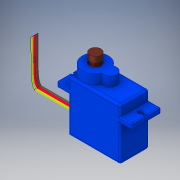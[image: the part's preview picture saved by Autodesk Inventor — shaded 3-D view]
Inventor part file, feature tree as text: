
AUTODESK INVENTOR PART (.ipt)
format: ipt  version: 2018 (Build 220112000, 112)  size: 405,504 bytes
history: native  units: in
note: dims shown in document units (in); Inventor stores cm internally (conversion verified against a paired STEP export)
features: sketch x10, extrude x9, fillet x2, plane x2, sweep x1
ambient origin geometry x8: Origin, YZ Plane, XZ Plane, XY Plane, X Axis, Y Axis, Z Axis, Center Point
bodies: Solid1 (feature_tree)
feature tree (24):
  extrude  "Servo_Body"  Depth=0.6102in
  extrude  "Cable_Opening"  Depth=0.0945in
  extrude  "GearBox_Housing"  Depth=0.4921in TaperAngle=0.0deg
  extrude  "Servo_Shaft"  Depth=0.0394in
  extrude  "GearBox_Housing_Extension"  Depth=0.4921in
  extrude  "Mounting_Holes"  Depth=0.0394in TaperAngle=0.0deg
  extrude  "Extrusion7"  Depth=0.189in
  fillet  "Fillet1"  Radius=0.1654in
  fillet  "Fillet2"  Radius=0.2205in
  extrude  "Cables"  Depth=0.1181in TaperAngle=0.0deg
  sweep  "Sweep1"
  plane  "Work Plane1"
  plane  "Work Plane2"
  extrude  "Shaft_Tapering"  Depth=0.0472in
  sketch  "Sketch1"  dims[d0=0.8898in d1=0.6102in]
  sketch  "Sketch2"  dims[d3=0.0945in d4=0.1969in]
  sketch  "Sketch4"  dims[d5=0.1732in d7=0.4921in d8=0.0in]
  sketch  "Sketch5"  dims[d9=0.1181in d10=0.0394in]
  sketch  "Sketch6"  dims[d11=0.1732in d12=0.4921in]
  sketch  "Sketch7"  dims[d13=0.2461in d14=0.0394in d15=0.0in]
  sketch  "Sketch8"  dims[d16=0.1654in d17=0.0in d18=0.189in d19=0.1654in d20=0.0in d21=0.2205in]
  sketch  "Sketch9"  dims[d22=0.2362in d23=0.1181in d24=0.0in]
  sketch  "Sketch10"  dims[d25=0.0787in d26=0.0787in]
  sketch  "Sketch11"  dims[d27=0.0886in d28=0.0886in d29=0.4921in d30=0.2461in d31=0.1181in d32=0.0in d33=0.0394in d35=0.0394in d36=0.4921in d37=0.2461in d38=0.1181in d39=0.0in d40=0.0394in d41=0.0197in d42=0.0787in d43=0.0394in d44=0.7874in d45=0.0in d46=0.0394in d47=0.0394in d48=0.0394in d49=0.0in d50=0.0in d51=0.0945in d52=1.2717in d53=0.6693in d54=0.4921in d55=0.2461in d56=-0.0984in d57=0.1654in d58=0.0472in d59=0.0in d60=0.1969in]
